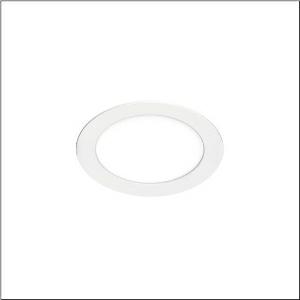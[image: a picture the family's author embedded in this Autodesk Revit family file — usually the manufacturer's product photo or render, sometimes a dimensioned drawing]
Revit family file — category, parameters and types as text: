
# Revit family: lunis_41_flat_51dr10dfgcb
name_source: partatom
category: Lighting Fixtures
units: mm (PartAtom-declared; Revit-internal decimal feet)

## family parameters
Cut with Voids When Loaded = No
Host = Face
Light Source = No
Part Type = Normal
Room Calculation Point = No
Round Connector Dimension = Use Diameter
Shared = No

## types (1)
- --- (1 x LED, 1550 lm, 11.5 W, 4000K)
    Apparent Load = 12 VA
    CIE Flux Codes = 49 80 96 100 100
    Color Rendering = 80
    Color Temperature = 4000K
    Default Elevation = 1800 mm
    Description = Lunis 41,  Flat, downlight, light emission: direct distribution, LED rated luminous flux: 2.050lm, light colour: 830/840, control gear: ECG, mains connection: 230V, AC, 50/60Hz, housing, round, of aluminium, coated, traffic white (RAL 9016), diameter: 225mm, protection rating (complete): IP20, protection rating (on room side): IP44, insulation class (complete): insulation class II (safety insulation), certification: CE, permissible ambient temperature for indoor applications: -20..+40°C, packaging unit: 1 piece
    Height = 0 mm  [stored 0 ft]
    Lamp = 1 x LED
    Lamp Light Flux = 1550 lm
    Lamp Power = 11.5 W
    Lamp count = 1
    Length = 225 mm
    Luminous efficacy = 135 lm/W
    Manufacturer = Siteco
    ModVariant = No
    Model = 51DR10DFGCB
    Mounting Place = Ceiling
    Mounting Type = Recessed
    Number of Poles = 1
    OnlyDefault = Yes
    Power Factor = 1
    Product Name = Lunis 41 Flat
    Product group = downlight
    ProductGroupID = 401
    Protection Class = Protection class II
    Protection Degree = IP 20
    RLX_Detail_Level = 1
    RLX_Emergency_Light_Flux = 0 lm
    RLX_Emergency_Type = 0
    RLX_Emergency_Type_DB = No
    RlxData = <blob elided: 13809 chars, md5=943248c3>
    Socket = socket
    Standby Power = 0 W
    System Light Flux = 1550 lm
    System Power = 12 W
    Type Comments = factory setting: colour temperature 4000K, luminous flux: 50 % | (ON | ON | ON) | 350 mA
    Type Image = l_1340923.jpg
    URL = http://relux.com
    VarID = @adj_002167
    Voltage = 0 V
    Weight = 0.00 kg
    Width = 0 mm  [stored 0 ft]

note: [stored X ft] marks values corroborated as IEEE doubles in the binary element streams (Revit-internal decimal feet)

## geometry (parser evidence)
native form markers: Sweep x10
no freeform markers — native parametric forms only
